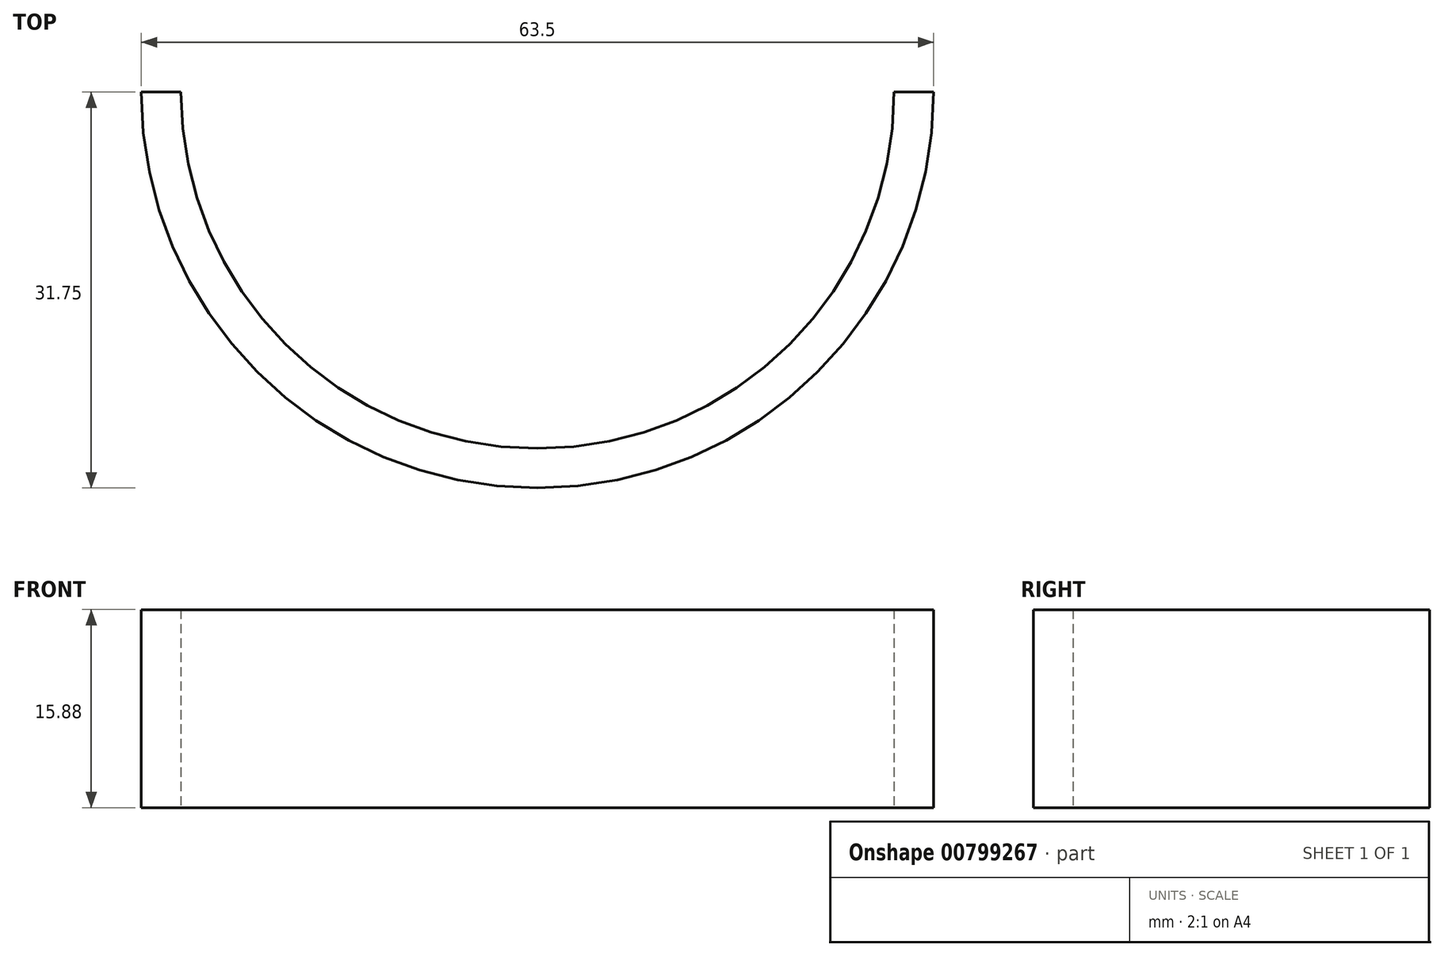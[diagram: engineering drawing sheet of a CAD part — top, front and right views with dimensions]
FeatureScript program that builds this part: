
annotation { "Feature Type Name" : "Feature", "Feature Type Description" : "" }
export const myFeature = defineFeature(function(context is Context, id is Id, definition is map)
    precondition{}
    {
        {
            var Q0;
            Q0=qCreatedBy(makeId("Top.planeOp"),FACE);
            var sketch = newSketch(context, id + "F0", { "sketchPlane" : qUnion([Q0])});
            skArc(sketch, "E0", {"start": v(-28.58, 0) * mm, "mid": v(0, -28.58) * mm, "end": v(28.58, 0) * mm});
            skArc(sketch, "E1.0", {"start": v(-31.75, 0) * mm, "mid": v(0, -31.75) * mm, "end": v(31.75, 0) * mm});
            skLineSegment(sketch, "E2", {"start": v(-31.75, 0) * mm, "end": v(-28.58, 0) * mm});
            skLineSegment(sketch, "E3", {"start": v(28.58, 0) * mm, "end": v(31.75, 0) * mm});
            skSolve(sketch);
        }
        {
            var Q0;
            Q0=makeQuery(id+"F0.imprint","IMPRINT",FACE,{"disambiguationData":[TD([[makeQuery(id+"F0.imprint","IMPRINT",EDGE,{"derivedFrom":sQuery(id+"F0.wireOp",EDGE,"E0")}),-1.0]])]});
            extrude(context, id + "F1", {"entities" : qUnion([Q0]), "depth" : 15.88 * mm, "offsetDistance" : 25.4 * mm});
        }
    });
